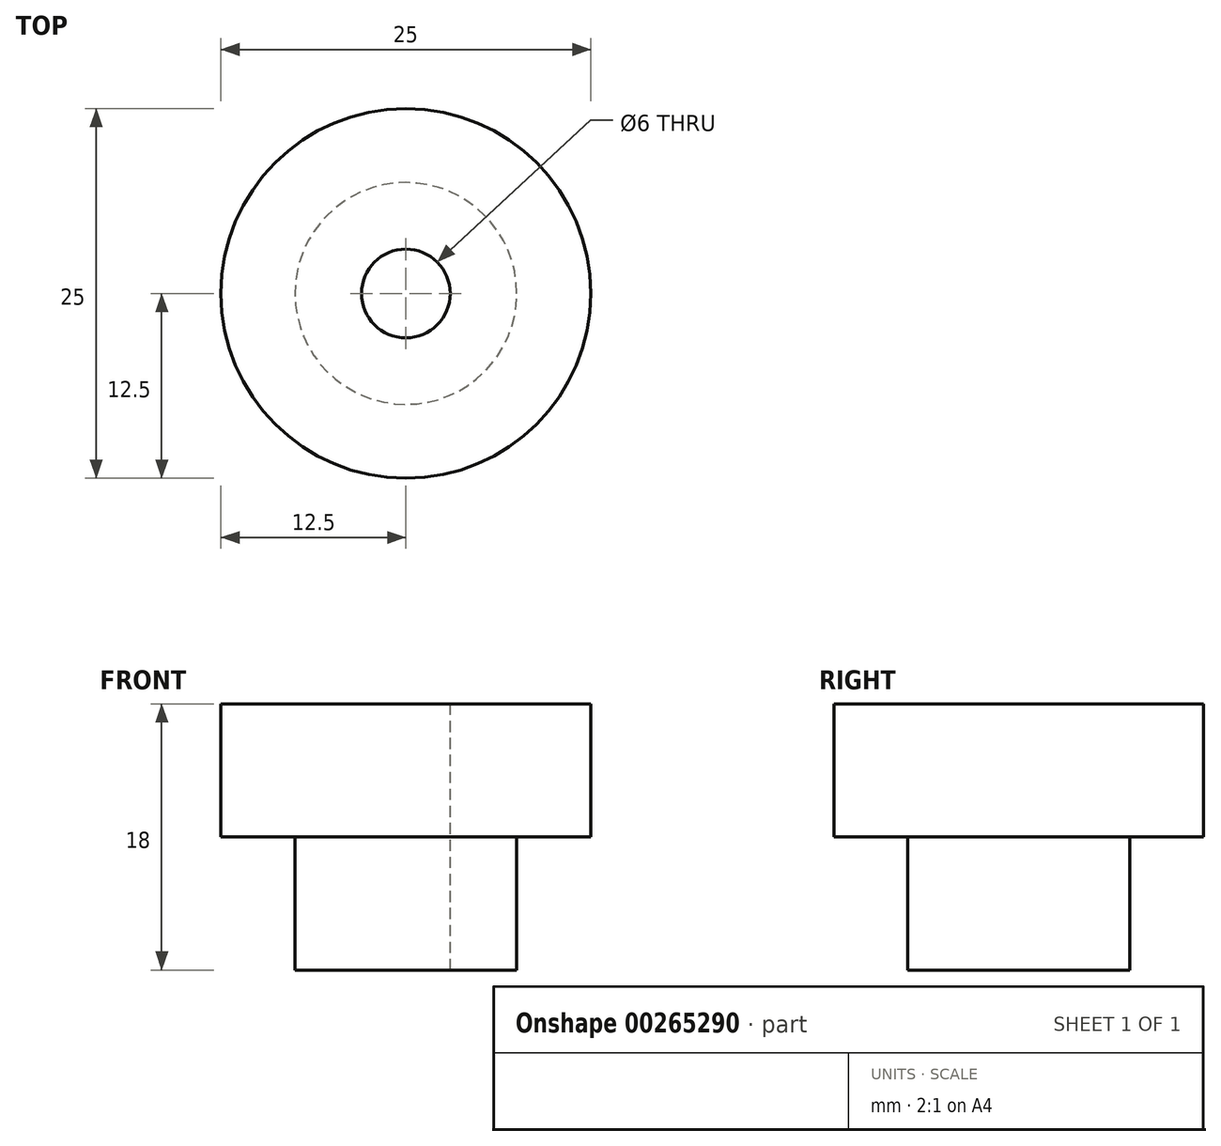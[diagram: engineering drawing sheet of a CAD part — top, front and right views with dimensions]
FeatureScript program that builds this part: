
annotation { "Feature Type Name" : "Feature", "Feature Type Description" : "" }
export const myFeature = defineFeature(function(context is Context, id is Id, definition is map)
    precondition{}
    {
        {
            var Q0;
            Q0=qCreatedBy(makeId("Right.planeOp"),FACE);
            var sketch = newSketch(context, id + "F0", { "sketchPlane" : qUnion([Q0])});
            skLineSegment(sketch, "E0", {"start": v(0, 0) * mm, "end": v(-3, 0) * mm, "construction": true});
            skLineSegment(sketch, "E1", {"start": v(-3, 0) * mm, "end": v(-12.5, 0) * mm});
            skLineSegment(sketch, "E2", {"start": v(-12.5, 0) * mm, "end": v(-12.5, -9) * mm});
            skLineSegment(sketch, "E3", {"start": v(-12.5, -9) * mm, "end": v(-7.5, -9) * mm});
            skLineSegment(sketch, "E4", {"start": v(-7.5, -9) * mm, "end": v(-7.5, -18) * mm});
            skLineSegment(sketch, "E5", {"start": v(-7.5, -18) * mm, "end": v(-3, -18) * mm});
            skLineSegment(sketch, "E6", {"start": v(-3, -18) * mm, "end": v(-3, 0) * mm});
            skLineSegment(sketch, "E7", {"start": v(0, 0) * mm, "end": v(0, -18.21) * mm, "construction": true});
            skSolve(sketch);
        }
        {
            var Q0;
            Q0=makeQuery(id+"F0.imprint","IMPRINT",FACE,{"disambiguationData":[TD([[makeQuery(id+"F0.imprint","IMPRINT",EDGE,{"derivedFrom":sQuery(id+"F0.wireOp",EDGE,"E1")}),1.0]])]});
            var Q1;
            Q1=sQuery(id+"F0.wireOp",EDGE,"E7");
            revolve(context, id + "F1", {"entities" : qUnion([Q0]), "axis" : qUnion([Q1]), "revolveType" : RevolveType.FULL});
        }
    });
